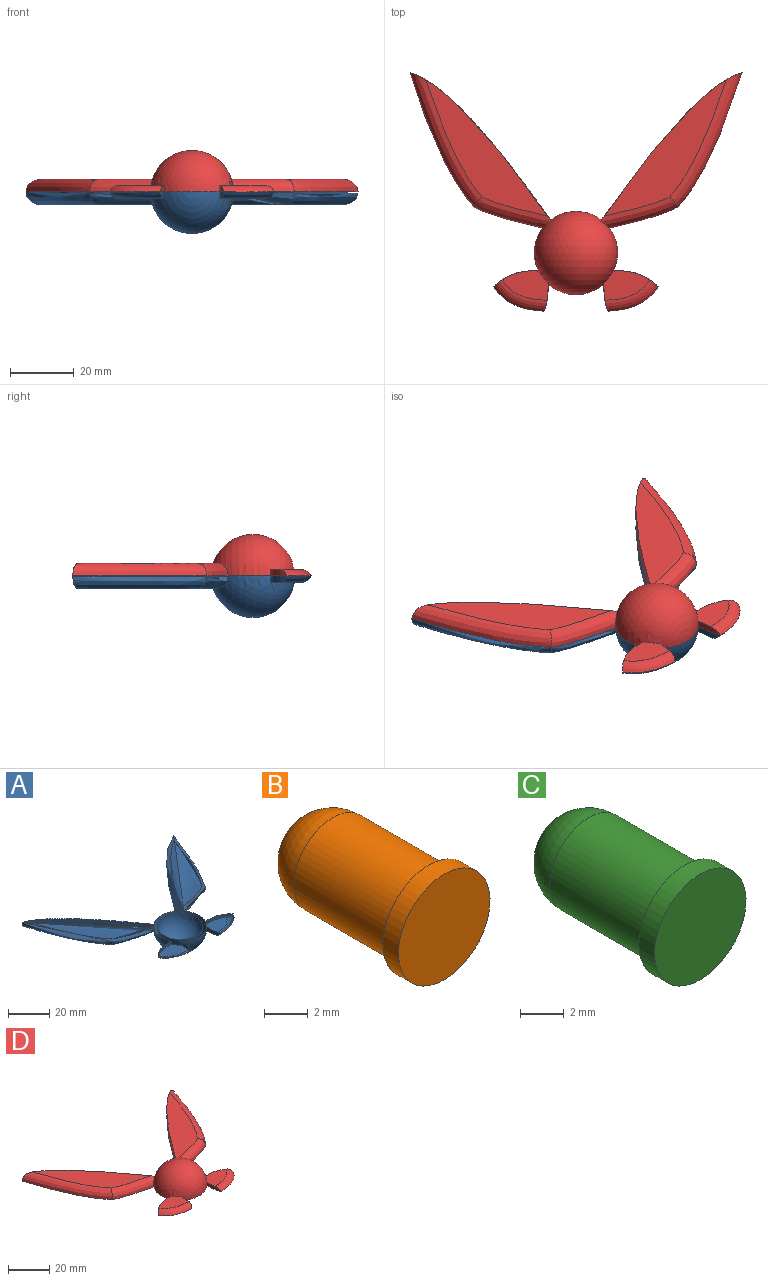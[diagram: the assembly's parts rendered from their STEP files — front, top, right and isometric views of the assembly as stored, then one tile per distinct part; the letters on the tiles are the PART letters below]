
ASSEMBLY  parts=4 mates=3
PART A: 27 faces, bbox 188x159.4x98.7 mm
  f0: plane 184.75x159.02mm, normal (0,0,-1), area -2266.2mm2, adj f1,f3,f4,f5,f7,f8,f9,f11
  f1: extruded ~43.33x38.91mm, area 111.1mm2, adj f0,f2,f3,f4
  f2: plane 39.24x34.52mm, normal (0,0,-1), area 370.3mm2, adj f1,f3,f4
  f3: bspline ~40.74x20.87mm, area 125mm2, adj f0,f1,f2,f4
  f4: bspline ~23.76x8.63mm, area 63.7mm2, adj f0,f1,f2,f3
  f5: bspline ~23.76x8.63mm, area 63.7mm2, adj f0,f6,f7,f8
  f6: plane 39.24x34.52mm, normal (0,0,1), area 370.3mm2, adj f5,f7,f8
  f7: extruded ~43.33x38.91mm, area 111.1mm2, adj f0,f5,f6,f8
  f8: bspline ~40.56x20.63mm, area 125mm2, adj f0,f5,f6,f7
  f9: extruded ~14.21x5.09mm, area 27.5mm2, adj f0,f10,f11,f21
  f10: plane 15.11x9.9mm, normal (0,0,-1), area 94.7mm2, adj f9,f11,f12,f21
  f11: bspline ~18.42x10.72mm, area 72.8mm2, adj f0,f9,f10,f12
  f12: extruded ~8.66x2mm, area 14.4mm2, adj f0,f10,f11,f21
  f13: extruded ~8.66x2mm, area 14.4mm2, adj f0,f14,f15,f21
  f14: plane 15.11x9.9mm, normal (0,0,-1), area 94.7mm2, adj f13,f15,f16,f21
  f15: bspline ~25.19x13.33mm, area 72.8mm2, adj f0,f13,f14,f16
  f16: extruded ~14.21x5.09mm, area 27.5mm2, adj f0,f14,f15,f21
  f17: extruded ~46.77x44.55mm, area 254.9mm2, adj f0,f18,f19,f20,f21
  f18: bspline ~26.75x11.03mm, area 145.7mm2, adj f17,f19,f20,f21
  f19: plane 47.18x42.64mm, normal (0,0,-1), area 480.7mm2, adj f17,f18,f20
  f20: bspline ~41.92x22.53mm, area 130.9mm2, adj f17,f18,f19
  f21: sphere r=13.08mm, area 1039.1mm2, adj f0,f9,f10,f12,f13,f14,f16,f17
  f22: bspline ~26.91x11.13mm, area 145.7mm2, adj f21,f23,f24,f25
  f23: plane 47.18x42.64mm, normal (0,0,-1), area 480.7mm2, adj f22,f24,f25
  f24: bspline ~42.1x22.78mm, area 130.9mm2, adj f22,f23,f25
  f25: extruded ~46.7x44.5mm, area 255.7mm2, adj f0,f21,f22,f23,f24
  f26: sphere r=11.08mm, area 771.4mm2, adj f0
PART B: 5 faces, bbox 5.9x9.7x5.9 mm
  f0: cylinder r=2.95mm len=5.9mm, axis (0,1,0), area 18.5mm2, adj f1,f2
  f1: plane 5.9x5.9mm, normal (0,-1,0), area 27.3mm2, adj f0
  f2: plane 5.9x5.9mm, normal (0,1,0), area 7.7mm2, adj f0,f3
  f3: cylinder r=2.5mm len=6.19mm, axis (0,-1,0), area 97.2mm2, adj f2,f4
  f4: sphere r=2.5mm, area 39.3mm2, adj f3
PART C: 5 faces, bbox 5.9x9.7x5.9 mm
  f0: cylinder r=2.95mm len=5.9mm, axis (0,1,0), area 18.5mm2, adj f1,f2
  f1: plane 5.9x5.9mm, normal (0,-1,0), area 27.3mm2, adj f0
  f2: plane 5.9x5.9mm, normal (0,1,0), area 7.7mm2, adj f0,f3
  f3: cylinder r=2.5mm len=6.19mm, axis (0,-1,0), area 97.2mm2, adj f2,f4
  f4: sphere r=2.5mm, area 39.3mm2, adj f3
PART D: 27 faces, bbox 106.8x80.8x16.2 mm
  f0: plane 105.45x76.48mm, normal (0,0,-1), area 976.9mm2, adj f1,f2,f4,f5,f6,f7,f9,f10
  f1: extruded ~46.7x44.5mm, area 255.7mm2, adj f0,f2,f3,f4,f5
  f2: bspline ~26.75x11.03mm, area 145.7mm2, adj f0,f1,f3,f4,f5
  f3: plane 47.18x42.64mm, normal (0,0,1), area 480.7mm2, adj f1,f2,f4
  f4: bspline ~46.25x24.11mm, area 277.9mm2, adj f0,f1,f2,f3
  f5: sphere r=13.08mm, area 1037mm2, adj f0,f1,f2,f6,f7,f10,f11,f12
  f6: extruded ~46.7x44.5mm, area 255.7mm2, adj f0,f5,f7,f8,f9
  f7: bspline ~26.91x11.13mm, area 145.7mm2, adj f0,f5,f6,f8,f9
  f8: plane 47.18x42.64mm, normal (0,0,1), area 480.7mm2, adj f6,f7,f9
  f9: bspline ~45.09x23.73mm, area 277.9mm2, adj f0,f6,f7,f8
  f10: extruded ~14.21x5.09mm, area 27.5mm2, adj f0,f5,f12,f13
  f11: extruded ~8.66x2mm, area 14.4mm2, adj f0,f5,f12,f13
  f12: plane 15.11x9.9mm, normal (0,0,1), area 94.7mm2, adj f5,f10,f11,f13
  f13: bspline ~25.19x13.33mm, area 72.8mm2, adj f0,f10,f11,f12
  f14: extruded ~8.66x2mm, area 14.4mm2, adj f0,f5,f16,f17
  f15: extruded ~14.21x5.09mm, area 27.5mm2, adj f0,f5,f16,f17
  f16: plane 15.11x9.9mm, normal (0,0,1), area 94.7mm2, adj f5,f14,f15,f17
  f17: bspline ~18.42x10.72mm, area 72.8mm2, adj f0,f14,f15,f16
  f18: sphere r=11.08mm, area 771.4mm2, adj f0
  f19: bspline ~40.74x20.87mm, area 125mm2, adj f0,f20,f21,f22
  f20: plane 39.24x34.52mm, normal (0,0,-1), area 370.3mm2, adj f19,f21,f22
  f21: bspline ~23.76x8.63mm, area 63.7mm2, adj f0,f19,f20,f22
  f22: extruded ~43.33x38.91mm, area 111.1mm2, adj f0,f19,f20,f21
  f23: extruded ~43.33x38.91mm, area 111.1mm2, adj f0,f24,f25,f26
  f24: bspline ~23.76x8.63mm, area 63.7mm2, adj f0,f23,f25,f26
  f25: plane 39.24x34.52mm, normal (0,0,-1), area 370.3mm2, adj f23,f24,f26
  f26: bspline ~40.56x20.63mm, area 125mm2, adj f0,f23,f24,f25
PLACE A t=(1.97,-46.46,42.76)mm
PLACE B rot(axis=(1,0,0),90deg) t=(-21.37,40.64,43.76)mm
PLACE C rot(axis=(1,0,0),90deg) t=(-14.77,40.64,43.76)mm
PLACE D t=(1.97,-46.46,42.76)mm
MATE fastened C.f0 <-> D.f0  axis (0,0,-1) through (-64.05,-19.53,42.76)mm
MATE fastened B.f0 <-> D.f0  axis (0,0,-1) through (-50.05,-19.53,42.76)mm
MATE fastened A.f0 <-> D.f0  axis (0,0,1) through (-57.05,-19.53,42.76)mm
